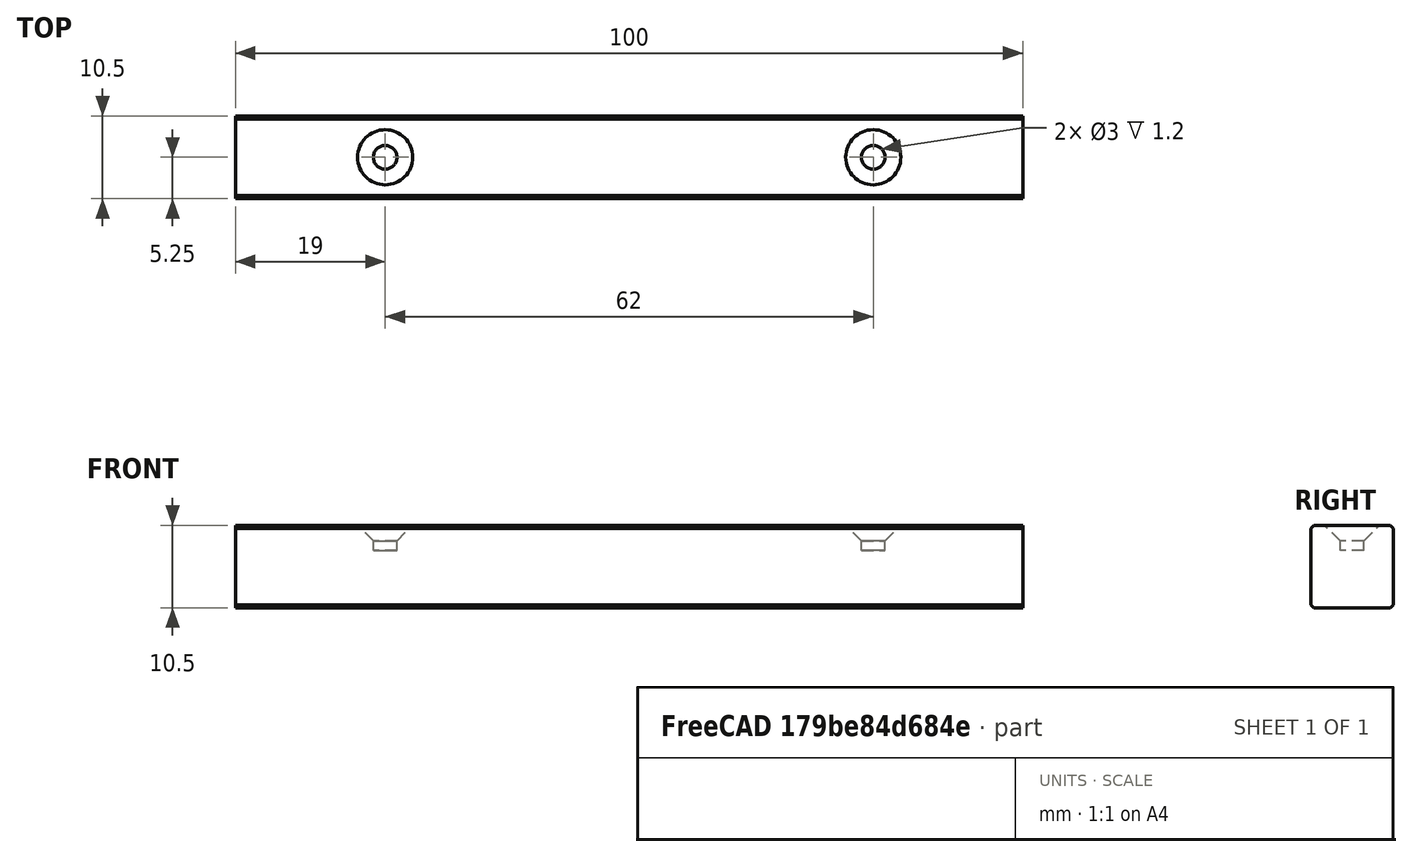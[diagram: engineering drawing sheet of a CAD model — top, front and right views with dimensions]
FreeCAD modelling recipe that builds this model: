
FCSTD DOCUMENT  (FreeCAD 1.0RUnknown)
Label: door-handle-bolt
License: All rights reserved
LicenseURL: https://en.wikipedia.org/wiki/All_rights_reserved
objects: Sketcher::SketchObject×2, PartDesign::Pad×1, PartDesign::Line×1, PartDesign::Plane×1, PartDesign::Groove×1, PartDesign::Mirrored×1, PartDesign::Chamfer×1, PartDesign::Body×1, Mesh::Feature×1
note: 18 computed .brp shape members not serialized (recipe doc carries the construction recipe); baked Part::Feature solids carry a one-line shape summary decoded from their .brp

FEATURE [Sketcher::SketchObject] Sketch
  ArcFitTolerance = 1e-06
  AttachmentSupport = -> [YZ_Plane]
  FullyConstrained = true
  MakeInternals = false
  MapMode = 5
  Placement = pos=(0,0,0) rot=(0.57735,0.57735,0.57735;2.0944rad)
  sketch-geometry (4):
    g0: LineSegment StartX=-5.25 StartY=5.25 StartZ=0 EndX=-5.25 EndY=-5.25 EndZ=0
    g1: LineSegment StartX=-5.25 StartY=-5.25 StartZ=0 EndX=5.25 EndY=-5.25 EndZ=0
    g2: LineSegment StartX=5.25 StartY=-5.25 StartZ=0 EndX=5.25 EndY=5.25 EndZ=0
    g3: LineSegment StartX=5.25 StartY=5.25 StartZ=0 EndX=-5.25 EndY=5.25 EndZ=0
  constraints (11):
    c: Coincident(g0,g1)
    c: Coincident(g1,g2)
    c: Coincident(g2,g3)
    c: Coincident(g3,g0)
    c: Vertical(g0)
    c: Vertical(g2)
    c: Horizontal(g1)
    c: Horizontal(g3)
    c: Symmetric(g0,g1,g-1)
    c: Equal(g0,g3)
    c: DistanceX(g3,g3) = 10.5
FEATURE [PartDesign::Pad] Pad
  Direction = (1,0,0)
  Length = 100
  Length2 = 10
  Midplane = true
  Placement = pos=(0,0,0) rot=(1,1,1;2.0944rad)
  Profile = -> Sketch
  ReferenceAxis = -> Sketch [N_Axis]
  Refine = true
  Suppressed = false
  Type = 0
FEATURE [PartDesign::Line] DatumLine
  AttacherType = Attacher::AttachEngineLine
  AttachmentOffset = pos=(31,0,0) rot=(0,0,1;0rad)
  AttachmentSupport = -> [Pad]
  Length = 20
  MapMode = 42
  Placement = pos=(31,-1.7e-15,0) rot=(0,0,1;0rad)
  ResizeMode = 0
FEATURE [PartDesign::Plane] DatumPlane
  AttachmentSupport = -> [DatumLine]
  Length = 60
  MapMode = 4
  Placement = pos=(31,-1.7e-15,0) rot=(0.57735,0.57735,0.57735;2.0944rad)
  ResizeMode = 0
  Width = 60
FEATURE [Sketcher::SketchObject] Sketch001
  ArcFitTolerance = 1e-06
  AttachmentSupport = -> [DatumPlane]
  ExternalGeometry = -> [Sketch]
  FullyConstrained = true
  MakeInternals = false
  MapMode = 5
  Placement = pos=(31,-1.7e-15,0) rot=(0.57735,0.57735,0.57735;2.0944rad)
  sketch-geometry (7):
    g0: LineSegment StartX=0 StartY=5.25 StartZ=0 EndX=0 EndY=2.05 EndZ=0
    g1: LineSegment StartX=0 StartY=2.05 StartZ=0 EndX=1.5 EndY=2.05 EndZ=0
    g2: LineSegment StartX=1.5 StartY=2.05 StartZ=0 EndX=1.5 EndY=3.25 EndZ=0
    g3: LineSegment StartX=1.5 StartY=3.25 StartZ=0 EndX=3.5 EndY=5.25 EndZ=0
    g4: LineSegment StartX=3.5 StartY=5.25 StartZ=0 EndX=0 EndY=5.25 EndZ=0
    g5: LineSegment [constr] StartX=1.5 StartY=3.25 StartZ=0 EndX=3.5 EndY=3.25 EndZ=0
    g6: LineSegment [constr] StartX=3.5 StartY=3.25 StartZ=0 EndX=3.5 EndY=5.25 EndZ=0
  constraints (20):
    c: PointOnObject(g4,g-3)
    c: Vertical(g0)
    c: Coincident(g1,g0)
    c: Vertical(g2)
    c: Coincident(g3,g2)
    c: PointOnObject(g3,g-3)
    c: Coincident(g4,g3)
    c: Coincident(g5,g2)
    c: Coincident(g6,g5)
    c: Coincident(g6,g3)
    c: Horizontal(g5)
    c: Vertical(g6)
    c: DistanceX(g1,g1) = 1.5
    c: DistanceY(g6,g6) = 2
    c: Distance(g2,g2) = 1.2
    c: Coincident(g1,g2)
    c: Equal(g6,g5)
    c: Coincident(g0,g4)
    c: PointOnObject(g0,g-2)
    c: Horizontal(g1)
FEATURE [PartDesign::Groove] Groove
  Angle = 360
  Angle2 = 60
  Axis = (0,0,1)
  Base = (31,-1.7e-15,0)
  BaseFeature = -> Pad
  Placement = pos=(0,0,0) rot=(1,1,1;2.0944rad)
  Profile = -> Sketch001
  ReferenceAxis = -> Sketch001 [V_Axis]
  Refine = true
  Suppressed = false
  Type = 0
FEATURE [PartDesign::Mirrored] Mirrored
  BaseFeature = -> Groove
  MirrorPlane = -> YZ_Plane
  Originals = -> [Groove]
  Placement = pos=(0,0,0) rot=(1,1,1;2.0944rad)
  Refine = true
  Suppressed = false
  TransformMode = 0
FEATURE [PartDesign::Chamfer] Chamfer
  Angle = 45
  Base = -> Mirrored [Edge1,Edge5,Edge2,Edge10]
  BaseFeature = -> Mirrored
  ChamferType = 0
  FlipDirection = false
  Placement = pos=(0,0,0) rot=(1,1,1;2.0944rad)
  Refine = true
  Size = 0.4
  Size2 = 1
  SupportTransform = false
  Suppressed = false
  UseAllEdges = false
FEATURE [PartDesign::Body] Body
  AllowCompound = false
  Group = -> [Sketch,Pad,DatumLine,DatumPlane,Sketch001,Groove,Mirrored,Chamfer]
  Origin = -> Origin
  Tip = -> Chamfer
FEATURE [Mesh::Feature] Mesh  label="Body (Meshed)"
